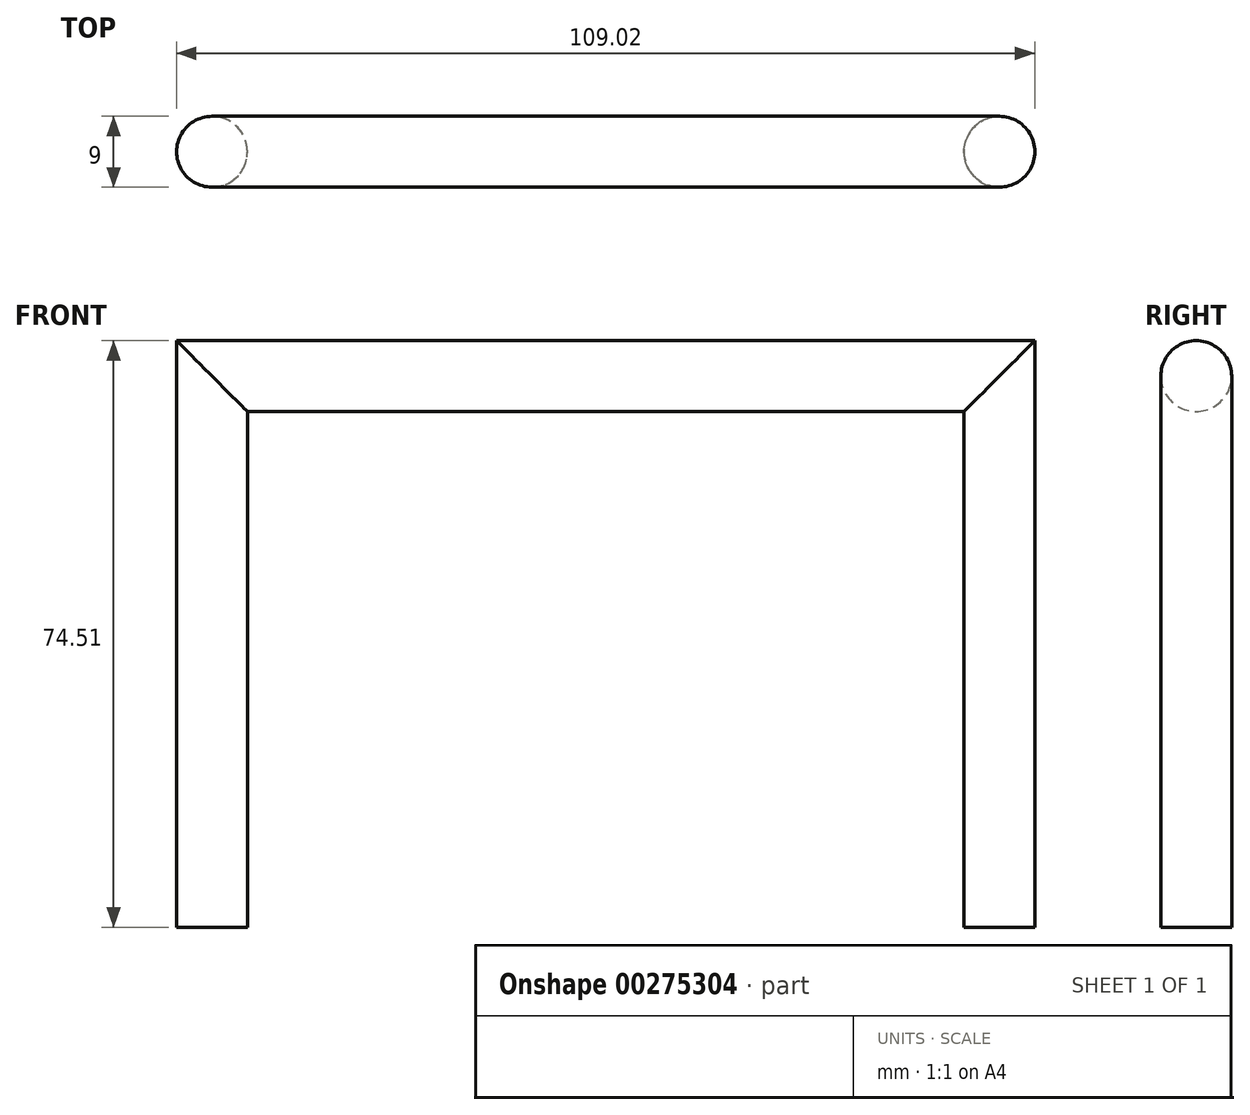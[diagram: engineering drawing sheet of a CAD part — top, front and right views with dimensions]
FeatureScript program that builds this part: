
annotation { "Feature Type Name" : "Feature", "Feature Type Description" : "" }
export const myFeature = defineFeature(function(context is Context, id is Id, definition is map)
    precondition{}
    {
        {
            var Q0;
            Q0=qCreatedBy(makeId("Front.planeOp"),FACE);
            var sketch = newSketch(context, id + "F0", { "sketchPlane" : qUnion([Q0])});
            skLineSegment(sketch, "E0.top", {"start": v(50, 35) * mm, "end": v(-50, 35) * mm});
            skLineSegment(sketch, "E0.left", {"start": v(50, -35) * mm, "end": v(50, 35) * mm});
            skLineSegment(sketch, "E0.right", {"start": v(-50, -35) * mm, "end": v(-50, 35) * mm});
            skPoint(sketch, "E0.middle", {"position": v(0, 0) * mm});
            skSolve(sketch);
        }
        {
            var Q0;
            Q0=qCreatedBy(makeId("Top.planeOp"),FACE);
            cPlane(context, id + "F1", {"entities" : qUnion([Q0]), "cplaneType" : CPlaneType.OFFSET, "offset" : 35 * mm, "oppositeDirection" : true, "width" : 150 * mm, "height" : 150 * mm});
        }
        {
            var Q0;
            Q0=qCreatedBy(id+"F1.planeOp",FACE);
            var sketch = newSketch(context, id + "F2", { "sketchPlane" : qUnion([Q0])});
            skCircle(sketch, "E1", {"center": v(-50.01, 0) * mm, "radius": 4.5 * mm});
            skSolve(sketch);
        }
        {
            var Q0;
            Q0=makeQuery(id+"F2.imprint","IMPRINT",FACE,{"disambiguationData":[TD([[makeQuery(id+"F2.imprint","IMPRINT",EDGE,{"derivedFrom":sQuery(id+"F2.wireOp",EDGE,"E1")}),1.0]])]});
            var Q1;
            Q1 = qConstructionFilter(qBodyType(qCreatedBy(id + "F0" ,EDGE), BodyType.WIRE), ConstructionObject.NO);
            sweep(context, id + "F3", {"profiles" : qUnion([Q0]), "path" : qUnion([Q1])});
        }
    });
